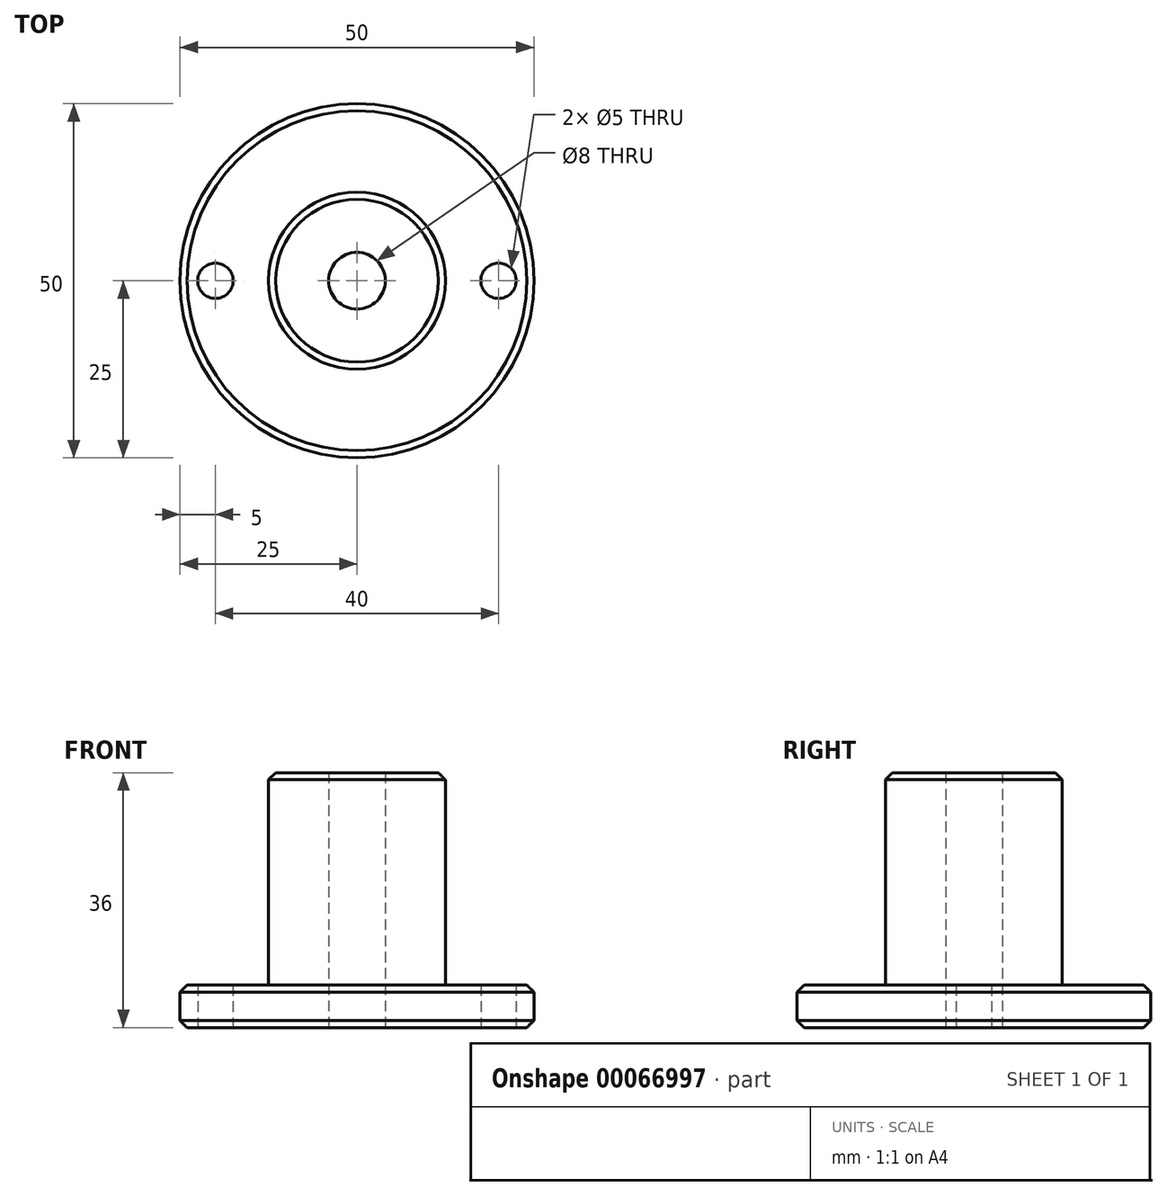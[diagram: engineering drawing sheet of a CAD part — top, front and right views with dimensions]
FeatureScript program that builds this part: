
annotation { "Feature Type Name" : "Feature", "Feature Type Description" : "" }
export const myFeature = defineFeature(function(context is Context, id is Id, definition is map)
    precondition{}
    {
        {
            var Q0;
            Q0=qCreatedBy(makeId("Top.planeOp"),FACE);
            var sketch = newSketch(context, id + "F0", { "sketchPlane" : qUnion([Q0])});
            skCircle(sketch, "E0", {"center": v(0, 0) * mm, "radius": 25 * mm});
            skCircle(sketch, "E1", {"center": v(0, 0) * mm, "radius": 4 * mm});
            skCircle(sketch, "E2", {"center": v(20, 0) * mm, "radius": 2.5 * mm});
            skCircle(sketch, "E3", {"center": v(-20, 0) * mm, "radius": 2.5 * mm});
            skSolve(sketch);
        }
        {
            var Q0;
            Q0 = qSketchRegion(id + "F0", true);
            extrude(context, id + "F1", {"entities" : qUnion([Q0]), "depth" : 6 * mm});
        }
        {
            var Q0;
            Q0=makeQuery(id+"F1.opExtrude","CAP_FACE",FACE,{"disambiguationData":[OSD([sQuery(id+"F0.wireOp",EDGE,"E0"),sQuery(id+"F0.wireOp",EDGE,"E1"),sQuery(id+"F0.wireOp",EDGE,"E2"),sQuery(id+"F0.wireOp",EDGE,"E3")])],"isStart":false});
            var sketch = newSketch(context, id + "F2", { "sketchPlane" : qUnion([Q0])});
            skCircle(sketch, "E4", {"center": v(0, 0) * mm, "radius": 4 * mm});
            skCircle(sketch, "E5", {"center": v(0, 0) * mm, "radius": 12.5 * mm});
            skSolve(sketch);
        }
        {
            var Q0;
            Q0 = qSketchRegion(id + "F2", true);
            extrude(context, id + "F3", {"entities" : qUnion([Q0]), "operationType" : NewBodyOperationType.ADD, "depth" : 30 * mm});
        }
        {
            var Q0;
            Q0=makeQuery(id+"F3.opExtrude","CAP_EDGE",EDGE,{"disambiguationData":[OSD([sQuery(id+"F2.wireOp",EDGE,"E5")])],"isStart":false});
            var Q1;
            Q1=makeQuery(id+"F1.opExtrude","CAP_EDGE",EDGE,{"disambiguationData":[OSD([sQuery(id+"F0.wireOp",EDGE,"E0")])],"isStart":false});
            var Q2;
            Q2=makeQuery(id+"F1.opExtrude","CAP_EDGE",EDGE,{"disambiguationData":[OSD([sQuery(id+"F0.wireOp",EDGE,"E0")])],"isStart":true});
            chamfer(context, id + "F4", {"entities" : qUnion([Q0, Q1, Q2]), "width" : 1 * mm, "tangentPropagation" : true});
        }
    });
